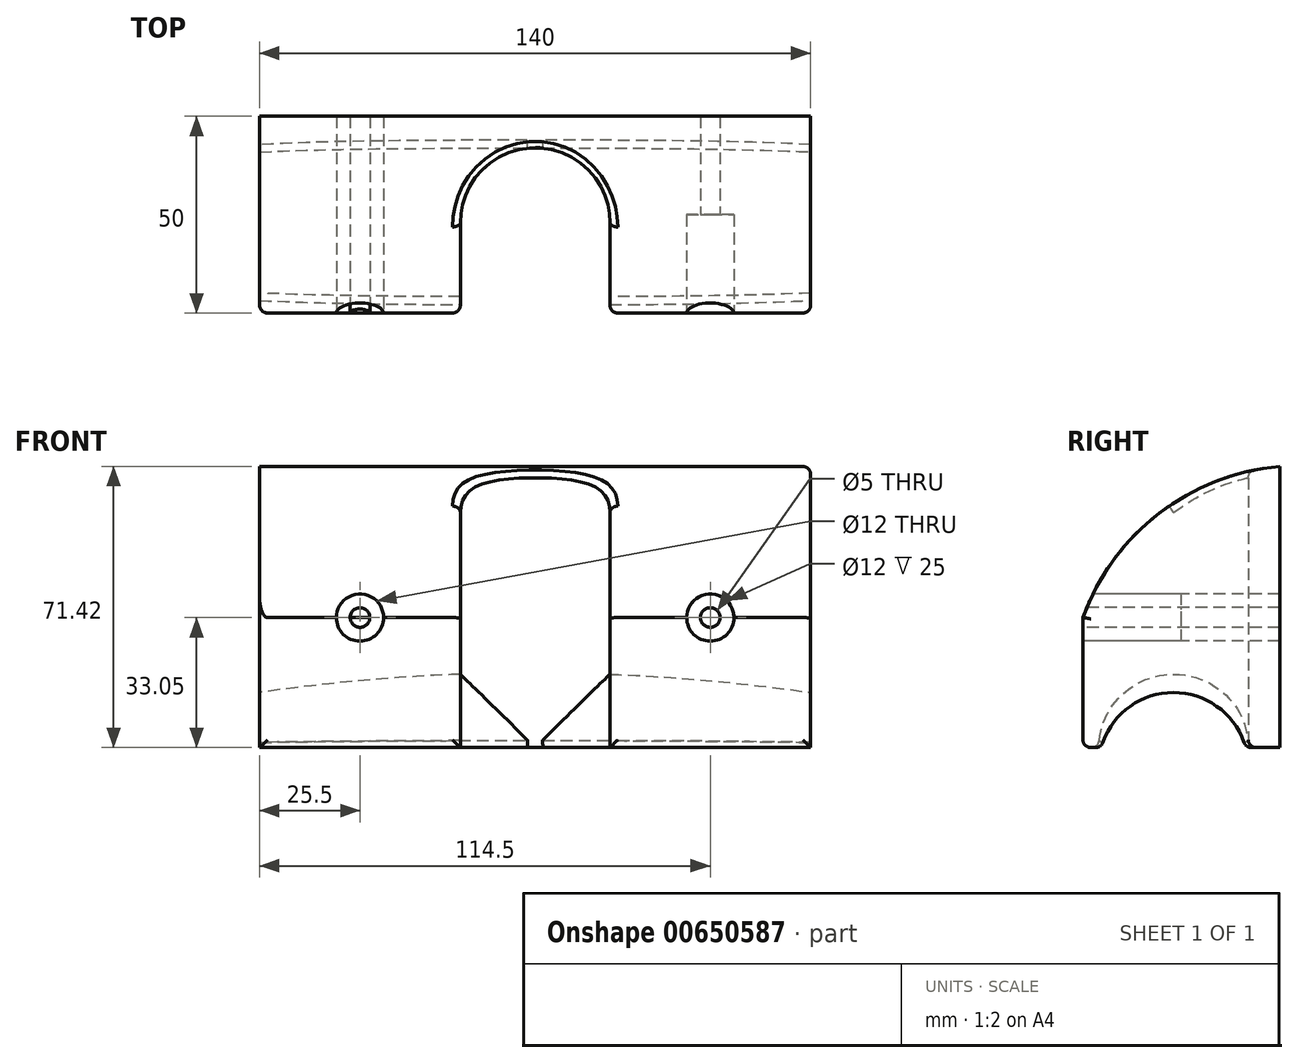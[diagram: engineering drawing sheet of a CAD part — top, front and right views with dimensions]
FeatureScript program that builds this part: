
annotation { "Feature Type Name" : "Feature", "Feature Type Description" : "" }
export const myFeature = defineFeature(function(context is Context, id is Id, definition is map)
    precondition{}
    {
        {
            var Q0;
            Q0=qCreatedBy(makeId("Top.planeOp"),FACE);
            var sketch = newSketch(context, id + "F0", { "sketchPlane" : qUnion([Q0])});
            skLineSegment(sketch, "E0.bottom", {"start": v(-70, -21.47) * mm, "end": v(70, -21.47) * mm});
            skLineSegment(sketch, "E0.top", {"start": v(-70, -71.47) * mm, "end": v(70, -71.47) * mm});
            skLineSegment(sketch, "E0.left", {"start": v(-70, -21.47) * mm, "end": v(-70, -71.47) * mm});
            skLineSegment(sketch, "E0.right", {"start": v(70, -21.47) * mm, "end": v(70, -71.47) * mm});
            skPoint(sketch, "E0.middle", {"position": v(0, -46.47) * mm});
            skSolve(sketch);
        }
        {
            var Q0;
            Q0 = qSketchRegion(id + "F0", true);
            extrude(context, id + "F1", {"entities" : qUnion([Q0]), "depth" : 80 * mm, "offsetDistance" : 25 * mm});
        }
        {
            var Q0;
            Q0=makeQuery(id+"F1.opExtrude","SWEPT_FACE",FACE,{"disambiguationData":[OSD([sQuery(id+"F0.wireOp",EDGE,"E0.top")])]});
            var sketch = newSketch(context, id + "F2", { "sketchPlane" : qUnion([Q0])});
            skArc(sketch, "E1", {"start": v(70, -10) * mm, "mid": v(0, -5) * mm, "end": v(-70, -10) * mm});
            skPoint(sketch, "E2", {"position": v(0, -5) * mm});
            skSolve(sketch);
        }
        {
            var Q0;
            Q0=makeQuery(id+"F1.opExtrude","SWEPT_FACE",FACE,{"disambiguationData":[OSD([sQuery(id+"F0.wireOp",EDGE,"E0.left")])]});
            var sketch = newSketch(context, id + "F3", { "sketchPlane" : qUnion([Q0])});
            skCircle(sketch, "E3", {"center": v(48.47, -5) * mm, "radius": 19 * mm});
            skSolve(sketch);
        }
        {
            var Q0;
            {var subQ0=sQuery(id+"F3.wireOp",EDGE,"E3");var subQ1=makeQuery(id+"F1.opExtrude","CAP_EDGE",EDGE,{"disambiguationData":[OSD([sQuery(id+"F0.wireOp",EDGE,"E0.left")])],"isStart":true});var subQ2=makeQuery(id+"F3.imprint","INTERSECT",VERTEX,{"disambiguationData":[OD(0.0)],"derivedFrom":[subQ1,subQ0]});Q0=makeQuery(id+"F3.imprint","IMPRINT",FACE,{"disambiguationData":[TD([[makeQuery(id+"F3.imprint","IMPRINT",EDGE,{"disambiguationData":[TD([[subQ2,1.0]])],"derivedFrom":subQ0}),1.0]])]});}
            var Q1;
            {var subQ0=sQuery(id+"F3.wireOp",EDGE,"E3");var subQ1=makeQuery(id+"F1.opExtrude","CAP_EDGE",EDGE,{"disambiguationData":[OSD([sQuery(id+"F0.wireOp",EDGE,"E0.left")])],"isStart":true});var subQ2=makeQuery(id+"F3.imprint","INTERSECT",VERTEX,{"disambiguationData":[OD(0.0)],"derivedFrom":[subQ1,subQ0]});Q1=makeQuery(id+"F3.imprint","IMPRINT",FACE,{"disambiguationData":[TD([[makeQuery(id+"F3.imprint","IMPRINT",EDGE,{"disambiguationData":[TD([[subQ2,-1.0]])],"derivedFrom":subQ0}),1.0]])]});}
            var Q2;
            Q2=sQuery(id+"F2.wireOp",EDGE,"E1");
            sweep(context, id + "F4", {"operationType" : NewBodyOperationType.REMOVE, "profiles" : qUnion([Q0, Q1]), "path" : qUnion([Q2]), "keepProfileOrientation" : true});
        }
        {
            var Q0;
            Q0=qCreatedBy(makeId("Top.planeOp"),FACE);
            var sketch = newSketch(context, id + "F5", { "sketchPlane" : qUnion([Q0])});
            skCircle(sketch, "E4", {"center": v(0, -48.47) * mm, "radius": 19 * mm});
            skLineSegment(sketch, "E5", {"start": v(19, -48.47) * mm, "end": v(19, -72.67) * mm});
            skLineSegment(sketch, "E6", {"start": v(-19, -48.47) * mm, "end": v(-19, -72.67) * mm});
            skLineSegment(sketch, "E7", {"start": v(-19, -72.67) * mm, "end": v(19, -72.67) * mm});
            skSolve(sketch);
        }
        {
            var Q0;
            Q0=makeQuery(id+"F5.imprint","IMPRINT",FACE,{"disambiguationData":[TD([[makeQuery(id+"F5.imprint","IMPRINT",EDGE,{"derivedFrom":sQuery(id+"F5.wireOp",EDGE,"E4")}),1.0]])]});
            var Q1;
            {var subQ0=sQuery(id+"F5.wireOp",EDGE,"E5");Q1=makeQuery(id+"F5.imprint","IMPRINT",FACE,{"disambiguationData":[TD([[makeQuery(id+"F5.imprint","IMPRINT",EDGE,{"derivedFrom":subQ0}),-1.0]])]});}
            extrude(context, id + "F6", {"entities" : qUnion([Q0, Q1]), "operationType" : NewBodyOperationType.REMOVE, "endBound" : BoundingType.THROUGH_ALL, "depth" : 25 * mm, "offsetDistance" : 25 * mm});
        }
        {
            var Q0;
            Q0=makeQuery(id+"F1.opExtrude","SWEPT_FACE",FACE,{"disambiguationData":[OSD([sQuery(id+"F0.wireOp",EDGE,"E0.left")])]});
            var sketch = newSketch(context, id + "F7", { "sketchPlane" : qUnion([Q0])});
            skArc(sketch, "E8", {"start": v(71.47, 33.05) * mm, "mid": v(52.08, 59.54) * mm, "end": v(21.47, 71.42) * mm});
            skLineSegment(sketch, "E9", {"start": v(21.47, 71.42) * mm, "end": v(21.47, 80) * mm});
            skLineSegment(sketch, "E10", {"start": v(21.47, 80) * mm, "end": v(71.47, 80) * mm});
            skLineSegment(sketch, "E11", {"start": v(71.47, 80) * mm, "end": v(71.47, 33.05) * mm});
            skSolve(sketch);
        }
        {
            var Q0;
            Q0 = qSketchRegion(id + "F7", true);
            extrude(context, id + "F8", {"entities" : qUnion([Q0]), "operationType" : NewBodyOperationType.REMOVE, "endBound" : BoundingType.THROUGH_ALL, "oppositeDirection" : true, "depth" : 25 * mm, "offsetDistance" : 25 * mm});
        }
        {
            var Q0;
            {var subQ0=sQuery(id+"F0.wireOp",EDGE,"E0.right");var subQ2=sQuery(id+"F0.wireOp",EDGE,"E0.top");Q0=makeQuery(id+"F6.boolean.opBoolean","SPLIT",FACE,{"disambiguationData":[TD([makeQuery(id+"F1.opExtrude","SWEPT_FACE",FACE,{"disambiguationData":[OSD([subQ0])]})])],"derivedFrom":makeQuery(id+"F1.opExtrude","SWEPT_FACE",FACE,{"disambiguationData":[OSD([subQ2])]})});}
            var sketch = newSketch(context, id + "F9", { "sketchPlane" : qUnion([Q0])});
            skCircle(sketch, "E12", {"center": v(44.5, 33.05) * mm, "radius": 6 * mm});
            skCircle(sketch, "E13", {"center": v(44.5, 33.05) * mm, "radius": 2.5 * mm});
            skCircle(sketch, "E14.MirrorC", {"center": v(-44.5, 33.05) * mm, "radius": 6 * mm});
            skCircle(sketch, "E15.MirrorC", {"center": v(-44.5, 33.05) * mm, "radius": 2.5 * mm});
            skSolve(sketch);
        }
        {
            var Q0;
            {var subQ0=sQuery(id+"F9.wireOp",EDGE,"E13");var subQ1=sQuery(id+"F0.wireOp",EDGE,"E0.top");var subQ2=sQuery(id+"F7.wireOp",EDGE,"E8");var subQ3=makeQuery(id+"F8.boolean.opBoolean","COPY",EDGE,{"disambiguationData":[TD([makeQuery(id+"F1.opExtrude","SWEPT_FACE",FACE,{"disambiguationData":[OSD([sQuery(id+"F0.wireOp",EDGE,"E0.right")])]})])],"derivedFrom":makeQuery(id+"F8.opExtrude","SWEPT_EDGE",EDGE,{"disambiguationData":[OSD([subQ1,sQuery(id+"F0.wireOp",EDGE,"E0.left"),subQ2,sQuery(id+"F7.wireOp",EDGE,"E11")])]})});var subQ4=makeQuery(id+"F9.imprint","INTERSECT",VERTEX,{"disambiguationData":[OD(0.0)],"derivedFrom":[subQ3,subQ0]});Q0=makeQuery(id+"F9.imprint","IMPRINT",FACE,{"disambiguationData":[TD([[makeQuery(id+"F9.imprint","IMPRINT",EDGE,{"disambiguationData":[TD([[subQ4,1.0]])],"derivedFrom":subQ0}),1.0]])]});}
            var Q1;
            {var subQ0=sQuery(id+"F9.wireOp",EDGE,"E13");var subQ1=sQuery(id+"F0.wireOp",EDGE,"E0.top");var subQ2=sQuery(id+"F7.wireOp",EDGE,"E8");var subQ3=makeQuery(id+"F8.boolean.opBoolean","COPY",EDGE,{"disambiguationData":[TD([makeQuery(id+"F1.opExtrude","SWEPT_FACE",FACE,{"disambiguationData":[OSD([sQuery(id+"F0.wireOp",EDGE,"E0.right")])]})])],"derivedFrom":makeQuery(id+"F8.opExtrude","SWEPT_EDGE",EDGE,{"disambiguationData":[OSD([subQ1,sQuery(id+"F0.wireOp",EDGE,"E0.left"),subQ2,sQuery(id+"F7.wireOp",EDGE,"E11")])]})});var subQ4=makeQuery(id+"F9.imprint","INTERSECT",VERTEX,{"disambiguationData":[OD(0.0)],"derivedFrom":[subQ3,subQ0]});Q1=makeQuery(id+"F9.imprint","IMPRINT",FACE,{"disambiguationData":[TD([[makeQuery(id+"F9.imprint","IMPRINT",EDGE,{"disambiguationData":[TD([[subQ4,-1.0]])],"derivedFrom":subQ0}),1.0]])]});}
            var Q2;
            Q2=makeQuery(id+"F9.imprint","IMPRINT",FACE,{"disambiguationData":[TD([[makeQuery(id+"F9.imprint","IMPRINT",EDGE,{"derivedFrom":sQuery(id+"F9.wireOp",EDGE,"E15.MirrorC")}),-1.0]])]});
            extrude(context, id + "F10", {"entities" : qUnion([Q0, Q1, Q2]), "operationType" : NewBodyOperationType.REMOVE, "endBound" : BoundingType.THROUGH_ALL, "oppositeDirection" : true, "depth" : 25 * mm, "offsetDistance" : 25 * mm});
        }
        {
            var Q0;
            {var subQ0=sQuery(id+"F9.wireOp",EDGE,"E12");var subQ1=sQuery(id+"F0.wireOp",EDGE,"E0.top");var subQ2=sQuery(id+"F7.wireOp",EDGE,"E8");var subQ3=makeQuery(id+"F8.boolean.opBoolean","COPY",EDGE,{"disambiguationData":[TD([makeQuery(id+"F1.opExtrude","SWEPT_FACE",FACE,{"disambiguationData":[OSD([sQuery(id+"F0.wireOp",EDGE,"E0.right")])]})])],"derivedFrom":makeQuery(id+"F8.opExtrude","SWEPT_EDGE",EDGE,{"disambiguationData":[OSD([subQ1,sQuery(id+"F0.wireOp",EDGE,"E0.left"),subQ2,sQuery(id+"F7.wireOp",EDGE,"E11")])]})});var subQ4=makeQuery(id+"F9.imprint","INTERSECT",VERTEX,{"disambiguationData":[OD(0.0)],"derivedFrom":[subQ3,subQ0]});Q0=makeQuery(id+"F9.imprint","IMPRINT",FACE,{"disambiguationData":[TD([[makeQuery(id+"F9.imprint","IMPRINT",EDGE,{"disambiguationData":[TD([[subQ4,1.0]])],"derivedFrom":subQ0}),1.0]])]});}
            var Q1;
            {var subQ0=sQuery(id+"F9.wireOp",EDGE,"E12");var subQ1=sQuery(id+"F0.wireOp",EDGE,"E0.top");var subQ2=sQuery(id+"F7.wireOp",EDGE,"E8");var subQ3=makeQuery(id+"F8.boolean.opBoolean","COPY",EDGE,{"disambiguationData":[TD([makeQuery(id+"F1.opExtrude","SWEPT_FACE",FACE,{"disambiguationData":[OSD([sQuery(id+"F0.wireOp",EDGE,"E0.right")])]})])],"derivedFrom":makeQuery(id+"F8.opExtrude","SWEPT_EDGE",EDGE,{"disambiguationData":[OSD([subQ1,sQuery(id+"F0.wireOp",EDGE,"E0.left"),subQ2,sQuery(id+"F7.wireOp",EDGE,"E11")])]})});var subQ4=makeQuery(id+"F9.imprint","INTERSECT",VERTEX,{"disambiguationData":[OD(0.0)],"derivedFrom":[subQ3,subQ0]});Q1=makeQuery(id+"F9.imprint","IMPRINT",FACE,{"disambiguationData":[TD([[makeQuery(id+"F9.imprint","IMPRINT",EDGE,{"disambiguationData":[TD([[subQ4,-1.0]])],"derivedFrom":subQ0}),1.0]])]});}
            var Q2;
            Q2=makeQuery(id+"F9.imprint","IMPRINT",FACE,{"disambiguationData":[TD([[makeQuery(id+"F9.imprint","IMPRINT",EDGE,{"derivedFrom":sQuery(id+"F9.wireOp",EDGE,"E14.MirrorC")}),-1.0]])]});
            extrude(context, id + "F11", {"entities" : qUnion([Q0, Q1, Q2]), "operationType" : NewBodyOperationType.REMOVE, "oppositeDirection" : true, "depth" : 25 * mm, "offsetDistance" : 25 * mm});
        }
        {
            var Q0;
            {var subQ0=sQuery(id+"F0.wireOp",EDGE,"E0.right");var subQ1=makeQuery(id+"F1.opExtrude","CAP_FACE",FACE,{"disambiguationData":[OSD([sQuery(id+"F0.wireOp",EDGE,"E0.bottom"),sQuery(id+"F0.wireOp",EDGE,"E0.top"),sQuery(id+"F0.wireOp",EDGE,"E0.left"),subQ0])],"isStart":true});var subQ2=makeQuery(id+"F4.opSweep","SWEPT_FACE",FACE,{"disambiguationData":[OSD([sQuery(id+"F2.wireOp",EDGE,"E1"),sQuery(id+"F3.wireOp",EDGE,"E3")])]});Q0=makeQuery(id+"F6.boolean.opBoolean","SPLIT",EDGE,{"disambiguationData":[TD([makeQuery(id+"F1.opExtrude","SWEPT_FACE",FACE,{"disambiguationData":[OSD([subQ0])]})])],"derivedFrom":makeQuery(id+"F4.boolean.opBoolean","INTERSECT",EDGE,{"disambiguationData":[OD(1.0)],"derivedFrom":[subQ1,subQ2]})});}
            var Q1;
            {var subQ0=sQuery(id+"F0.wireOp",EDGE,"E0.left");var subQ1=makeQuery(id+"F1.opExtrude","CAP_FACE",FACE,{"disambiguationData":[OSD([sQuery(id+"F0.wireOp",EDGE,"E0.bottom"),sQuery(id+"F0.wireOp",EDGE,"E0.top"),subQ0,sQuery(id+"F0.wireOp",EDGE,"E0.right")])],"isStart":true});var subQ2=makeQuery(id+"F4.opSweep","SWEPT_FACE",FACE,{"disambiguationData":[OSD([sQuery(id+"F2.wireOp",EDGE,"E1"),sQuery(id+"F3.wireOp",EDGE,"E3")])]});Q1=makeQuery(id+"F6.boolean.opBoolean","SPLIT",EDGE,{"disambiguationData":[TD([makeQuery(id+"F1.opExtrude","SWEPT_FACE",FACE,{"disambiguationData":[OSD([subQ0])]})])],"derivedFrom":makeQuery(id+"F4.boolean.opBoolean","INTERSECT",EDGE,{"disambiguationData":[OD(1.0)],"derivedFrom":[subQ1,subQ2]})});}
            var Q2;
            {var subQ0=sQuery(id+"F0.wireOp",EDGE,"E0.left");var subQ1=sQuery(id+"F0.wireOp",EDGE,"E0.top");Q2=makeQuery(id+"F6.boolean.opBoolean","SPLIT",EDGE,{"disambiguationData":[TD([makeQuery(id+"F1.opExtrude","SWEPT_FACE",FACE,{"disambiguationData":[OSD([subQ0])]})])],"derivedFrom":makeQuery(id+"F1.opExtrude","CAP_EDGE",EDGE,{"disambiguationData":[OSD([subQ1])],"isStart":true})});}
            var Q3;
            {var subQ0=sQuery(id+"F0.wireOp",EDGE,"E0.right");var subQ1=sQuery(id+"F0.wireOp",EDGE,"E0.top");Q3=makeQuery(id+"F6.boolean.opBoolean","SPLIT",EDGE,{"disambiguationData":[TD([makeQuery(id+"F1.opExtrude","SWEPT_FACE",FACE,{"disambiguationData":[OSD([subQ0])]})])],"derivedFrom":makeQuery(id+"F1.opExtrude","CAP_EDGE",EDGE,{"disambiguationData":[OSD([subQ1])],"isStart":true})});}
            var Q4;
            Q4=makeQuery(id+"F6.boolean.opBoolean","INTERSECT",EDGE,{"derivedFrom":[makeQuery(id+"F1.opExtrude","SWEPT_FACE",FACE,{"disambiguationData":[OSD([sQuery(id+"F0.wireOp",EDGE,"E0.top")])]}),makeQuery(id+"F6.opExtrude","SWEPT_FACE",FACE,{"disambiguationData":[OSD([sQuery(id+"F5.wireOp",EDGE,"E5")])]})]});
            var Q5;
            Q5=makeQuery(id+"F6.boolean.opBoolean","INTERSECT",EDGE,{"derivedFrom":[makeQuery(id+"F1.opExtrude","SWEPT_FACE",FACE,{"disambiguationData":[OSD([sQuery(id+"F0.wireOp",EDGE,"E0.top")])]}),makeQuery(id+"F6.opExtrude","SWEPT_FACE",FACE,{"disambiguationData":[OSD([sQuery(id+"F5.wireOp",EDGE,"E6")])]})]});
            var Q6;
            Q6=makeQuery(id+"F8.boolean.opBoolean","INTERSECT",EDGE,{"derivedFrom":[makeQuery(id+"F6.boolean.opBoolean","COPY",FACE,{"derivedFrom":makeQuery(id+"F6.opExtrude","SWEPT_FACE",FACE,{"disambiguationData":[OSD([sQuery(id+"F5.wireOp",EDGE,"E5")])]})}),makeQuery(id+"F8.opExtrude","SWEPT_FACE",FACE,{"disambiguationData":[OSD([sQuery(id+"F7.wireOp",EDGE,"E8")])]})]});
            var Q7;
            Q7=makeQuery(id+"F8.boolean.opBoolean","INTERSECT",EDGE,{"derivedFrom":[makeQuery(id+"F6.boolean.opBoolean","COPY",FACE,{"derivedFrom":makeQuery(id+"F6.opExtrude","SWEPT_FACE",FACE,{"disambiguationData":[OSD([sQuery(id+"F5.wireOp",EDGE,"E6")])]})}),makeQuery(id+"F8.opExtrude","SWEPT_FACE",FACE,{"disambiguationData":[OSD([sQuery(id+"F7.wireOp",EDGE,"E8")])]})]});
            var Q8;
            Q8=makeQuery(id+"F1.opExtrude","SWEPT_EDGE",EDGE,{"disambiguationData":[OSD([sQuery(id+"F0.wireOp",EDGE,"E0.top"),sQuery(id+"F0.wireOp",EDGE,"E0.left")])]});
            var Q9;
            Q9=makeQuery(id+"F8.boolean.opBoolean","COPY",EDGE,{"derivedFrom":makeQuery(id+"F8.opExtrude","CAP_EDGE",EDGE,{"disambiguationData":[OSD([sQuery(id+"F7.wireOp",EDGE,"E8")])],"isStart":true})});
            var Q10;
            Q10=makeQuery(id+"F1.opExtrude","SWEPT_EDGE",EDGE,{"disambiguationData":[OSD([sQuery(id+"F0.wireOp",EDGE,"E0.top"),sQuery(id+"F0.wireOp",EDGE,"E0.right")])]});
            var Q11;
            Q11=makeQuery(id+"F8.boolean.opBoolean","INTERSECT",EDGE,{"derivedFrom":[makeQuery(id+"F1.opExtrude","SWEPT_FACE",FACE,{"disambiguationData":[OSD([sQuery(id+"F0.wireOp",EDGE,"E0.right")])]}),makeQuery(id+"F8.opExtrude","SWEPT_FACE",FACE,{"disambiguationData":[OSD([sQuery(id+"F7.wireOp",EDGE,"E8")])]})]});
            var Q12;
            {var subQ0=sQuery(id+"F0.wireOp",EDGE,"E0.right");var subQ1=makeQuery(id+"F1.opExtrude","CAP_FACE",FACE,{"disambiguationData":[OSD([sQuery(id+"F0.wireOp",EDGE,"E0.bottom"),sQuery(id+"F0.wireOp",EDGE,"E0.top"),sQuery(id+"F0.wireOp",EDGE,"E0.left"),subQ0])],"isStart":true});var subQ2=makeQuery(id+"F4.opSweep","SWEPT_FACE",FACE,{"disambiguationData":[OSD([sQuery(id+"F2.wireOp",EDGE,"E1"),sQuery(id+"F3.wireOp",EDGE,"E3")])]});Q12=makeQuery(id+"F6.boolean.opBoolean","SPLIT",EDGE,{"disambiguationData":[TD([makeQuery(id+"F1.opExtrude","SWEPT_FACE",FACE,{"disambiguationData":[OSD([subQ0])]})])],"derivedFrom":makeQuery(id+"F4.boolean.opBoolean","INTERSECT",EDGE,{"disambiguationData":[OD(0.0)],"derivedFrom":[subQ1,subQ2]})});}
            fillet(context, id + "F12", {"entities" : qUnion([Q0, Q1, Q2, Q3, Q4, Q5, Q6, Q7, Q8, Q9, Q10, Q11, Q12]), "radius" : 2 * mm, "tangentPropagation" : true, "allowEdgeOverflow" : false});
        }
    });
